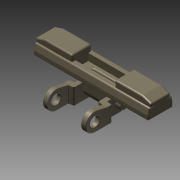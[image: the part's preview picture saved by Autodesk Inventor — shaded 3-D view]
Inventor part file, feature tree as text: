
AUTODESK INVENTOR PART (.ipt)
format: ipt  version: 2013 (Build 170138000, 138)  size: 529,408 bytes
history: native  units: in
note: dims shown in document units (in); Inventor stores cm internally (conversion verified against a paired STEP export)
features: fillet x14, sketch x13, extrude x12, plane x8, mirror x3, projected_geometry x2, hole x1
ambient origin geometry x8: Origin, YZ Plane, XZ Plane, XY Plane, X Axis, Y Axis, Z Axis, Center Point
bodies: Solid1 (feature_tree)
feature tree (53):
  extrude  "Extrusion1"  Depth=0.3268in
  plane  "Work Plane1"
  fillet  "Fillet1"  Radius=0.061in
  extrude  "Extrusion2"  Depth=0.244in
  plane  "Work Plane2"
  extrude  "Extrusion4"  Depth=0.224in
  plane  "Work Plane3"
  extrude  "Extrusion7"  Depth=0.0591in TaperAngle=0.0deg
  extrude  "Extrusion9"  Depth=0.0021in
  fillet  "Fillet5"  Radius=0.1634in
  fillet  "Fillet6"  Radius=0.0453in
  fillet  "Fillet7"  Radius=0.1634in
  hole  "Hole1"  [1 undecoded]
  fillet  "Fillet8"  Radius=0.6205in
  fillet  "Fillet9"  Radius=0.0984in
  plane  "Work Plane4"
  mirror  "Mirror1"
  fillet  "Fillet10"  Radius=0.1181in
  extrude  "Extrusion11"  Depth=0.063in TaperAngle=0.0deg
  extrude  "Extrusion12"  Depth=0.0079in
  plane  "Work Plane7"
  extrude  "Extrusion13"  Depth=0.0079in
  fillet  "Fillet12"  Radius=0.0079in
  mirror  "Mirror2"
  extrude  "Extrusion14"  Depth=0.0197in
  fillet  "Fillet14"  Radius=0.258in
  fillet  "Fillet15"  Radius=0.1181in
  plane  "Work Plane8"
  extrude  "Extrusion16"  Depth=0.0392in
  fillet  "Fillet16"  Radius=0.066in
  extrude  "Extrusion17"  Depth=0.0197in
  mirror  "Mirror3"
  extrude  "Extrusion18"  Depth=1.0625in TaperAngle=0.0deg
  fillet  "Fillet17"  Radius=0.0591in
  fillet  "Fillet18"  Radius=0.126in
  fillet  "Fillet19"  Radius=0.122in
  sketch  "Sketch1"  dims[d0=1.4961in d1=0.3268in d2=0.061in d3=0.0in]
  sketch  "Sketch2"  dims[d5=0.315in d6=0.0in d10=0.244in]
  sketch  "Sketch6"  dims[d11=0.2362in d12=0.224in]
  sketch  "Sketch10"  dims[d13=0.087in d15=0.0591in d16=0.0in]
  sketch  "Sketch11"  dims[d17=0.063in d27=0.0021in d28=0.1634in d29=0.0453in d30=0.1634in]
  sketch  "Sketch13"  dims[d31=0.126in d32=0.6205in d33=0.6205in d34=0.0984in d35=0.1181in]
  plane  "Work Plane5"
  plane  "Work Plane6"
  sketch  "Sketch15"  dims[d38=0.3858in d39=0.063in d40=0.0591in d41=0.0in d42=0.0in]
  sketch  "Sketch16"  dims[d49=0.063in d50=0.0in d51=0.0079in d52=0.02in]
  sketch  "Sketch17"  dims[d53=0.0079in d54=0.0079in]
  sketch  "Sketch18"  dims[d55=0.122in d56=0.75in d57=0.375in d58=0.25in d59=0.5635in d60=1.0in d61=0.8108in d62=0.0079in]
  sketch  "Sketch19"  dims[d63=0.0787in d64=0.0197in d69=0.258in d70=-0.0034in d72=0.1181in]
  projected_geometry  "Projected Loop3"
  projected_geometry  "Projected Loop4"
  sketch  "Sketch20"  dims[d73=0.0669in d74=0.0in d75=0.0392in d76=0.066in d77=0.0in]
  sketch  "Sketch21"  dims[d78=0.008in d79=0.0197in d80=1.0625in d81=0.0in d86=0.0591in d87=0.126in d89=0.122in d99=0.2559in d100=0.0in d101=0.315in d102=1.1404in d103=1.1404in d104=0.1378in d105=0.2165in d106=1.1102in d107=0.1245in d108=0.4724in d109=0.0197in d110=0.0197in d111=0.0197in d112=0.1654in d113=0.0in d114=0.1654in d115=0.0906in d116=0.0in d117=0.0118in d118=0.0197in]
note: 1 required parameter value undecoded (feature->parameter linkage not recoverable at this tier; creation-order binding heuristic only, values carry confidence <= 0.55)
